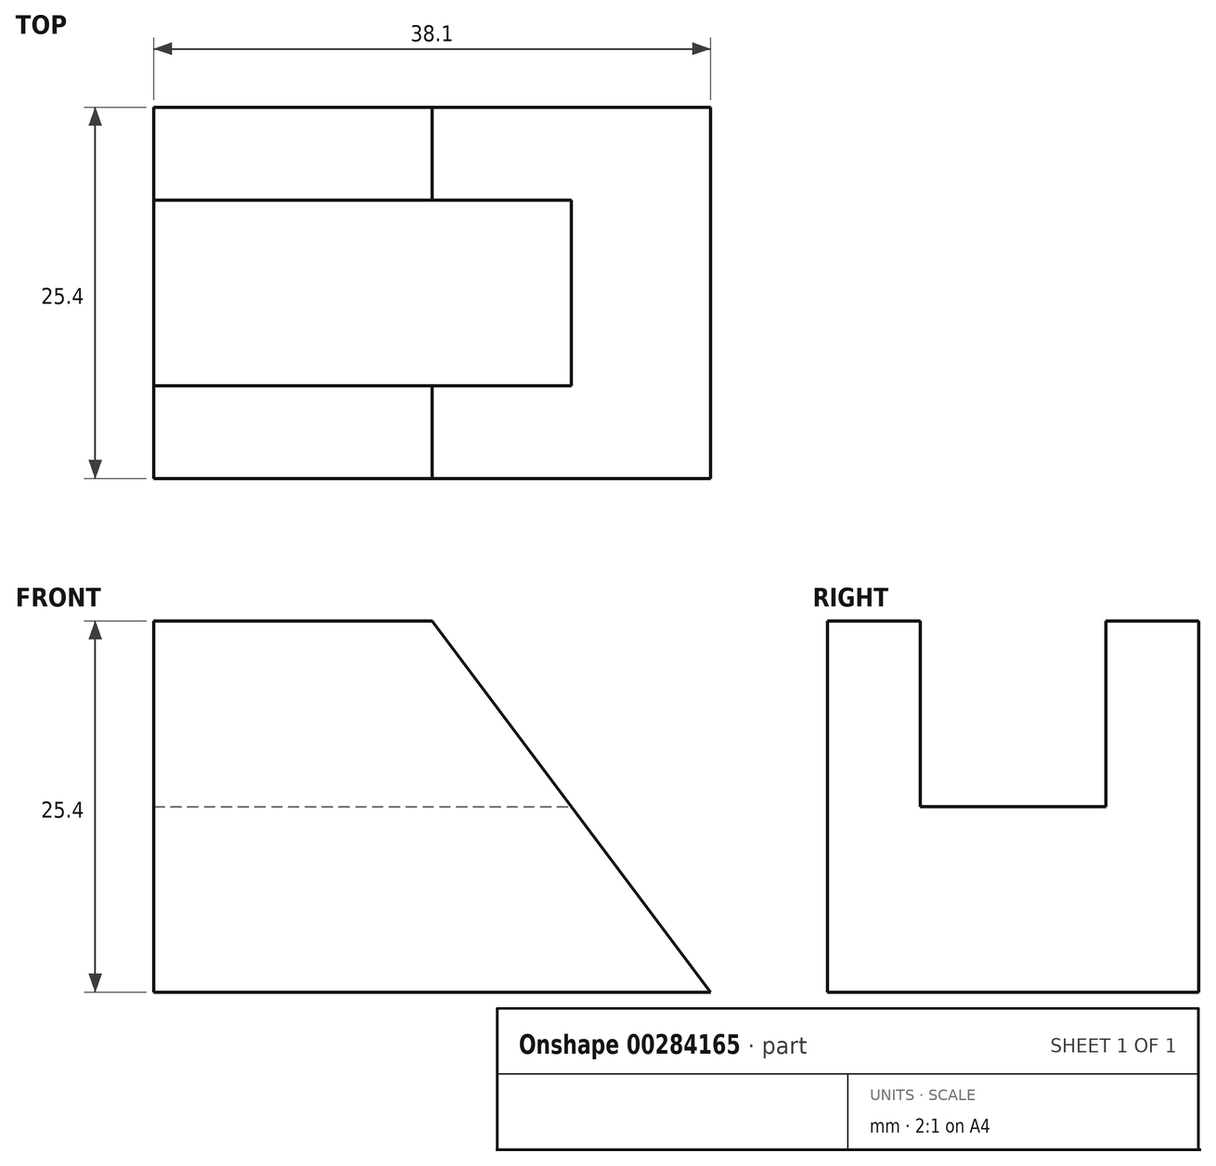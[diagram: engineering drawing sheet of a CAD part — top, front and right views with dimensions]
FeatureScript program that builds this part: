
annotation { "Feature Type Name" : "Feature", "Feature Type Description" : "" }
export const myFeature = defineFeature(function(context is Context, id is Id, definition is map)
    precondition{}
    {
        {
            var Q0;
            Q0=qCreatedBy(makeId("Front.planeOp"),FACE);
            var sketch = newSketch(context, id + "F0", { "sketchPlane" : qUnion([Q0])});
            skLineSegment(sketch, "E0.bottom", {"start": v(0, 0) * mm, "end": v(38.1, 0) * mm});
            skLineSegment(sketch, "E0.top", {"start": v(0, 25.4) * mm, "end": v(19.05, 25.4) * mm});
            skLineSegment(sketch, "E0.left", {"start": v(0, 0) * mm, "end": v(0, 25.4) * mm});
            skPoint(sketch, "E1", {"position": v(0, 25.4) * mm});
            skLineSegment(sketch, "E2", {"start": v(19.05, 25.4) * mm, "end": v(38.1, 0) * mm});
            skSolve(sketch);
        }
        {
            var Q0;
            Q0 = qSketchRegion(id + "F0", true);
            extrude(context, id + "F1", {"entities" : qUnion([Q0]), "depth" : 25.4 * mm});
        }
        {
            var Q0;
            Q0=makeQuery(id+"F1.opExtrude","SWEPT_FACE",FACE,{"disambiguationData":[OSD([sQuery(id+"F0.wireOp",EDGE,"E0.top")])]});
            var sketch = newSketch(context, id + "F2", { "sketchPlane" : qUnion([Q0])});
            skLineSegment(sketch, "E3.bottom", {"start": v(0, -6.35) * mm, "end": v(19.05, -6.35) * mm});
            skLineSegment(sketch, "E3.top", {"start": v(0, -19.05) * mm, "end": v(19.05, -19.05) * mm});
            skLineSegment(sketch, "E3.left", {"start": v(0, -6.35) * mm, "end": v(0, -19.05) * mm});
            skLineSegment(sketch, "E3.right", {"start": v(19.05, -6.35) * mm, "end": v(19.05, -19.05) * mm});
            skSolve(sketch);
        }
        {
            var Q0;
            Q0 = qSketchRegion(id + "F2", true);
            extrude(context, id + "F3", {"entities" : qUnion([Q0]), "operationType" : NewBodyOperationType.REMOVE, "oppositeDirection" : true, "depth" : 12.7 * mm});
        }
        {
            var Q0;
            Q0=makeQuery(id+"F3.boolean.opBoolean","COPY",FACE,{"derivedFrom":makeQuery(id+"F3.opExtrude","SWEPT_FACE",FACE,{"disambiguationData":[OSD([sQuery(id+"F2.wireOp",EDGE,"E3.right")])]})});
            extrude(context, id + "F4", {"entities" : qUnion([Q0]), "operationType" : NewBodyOperationType.REMOVE, "oppositeDirection" : true, "depth" : 25.4 * mm});
        }
    });
